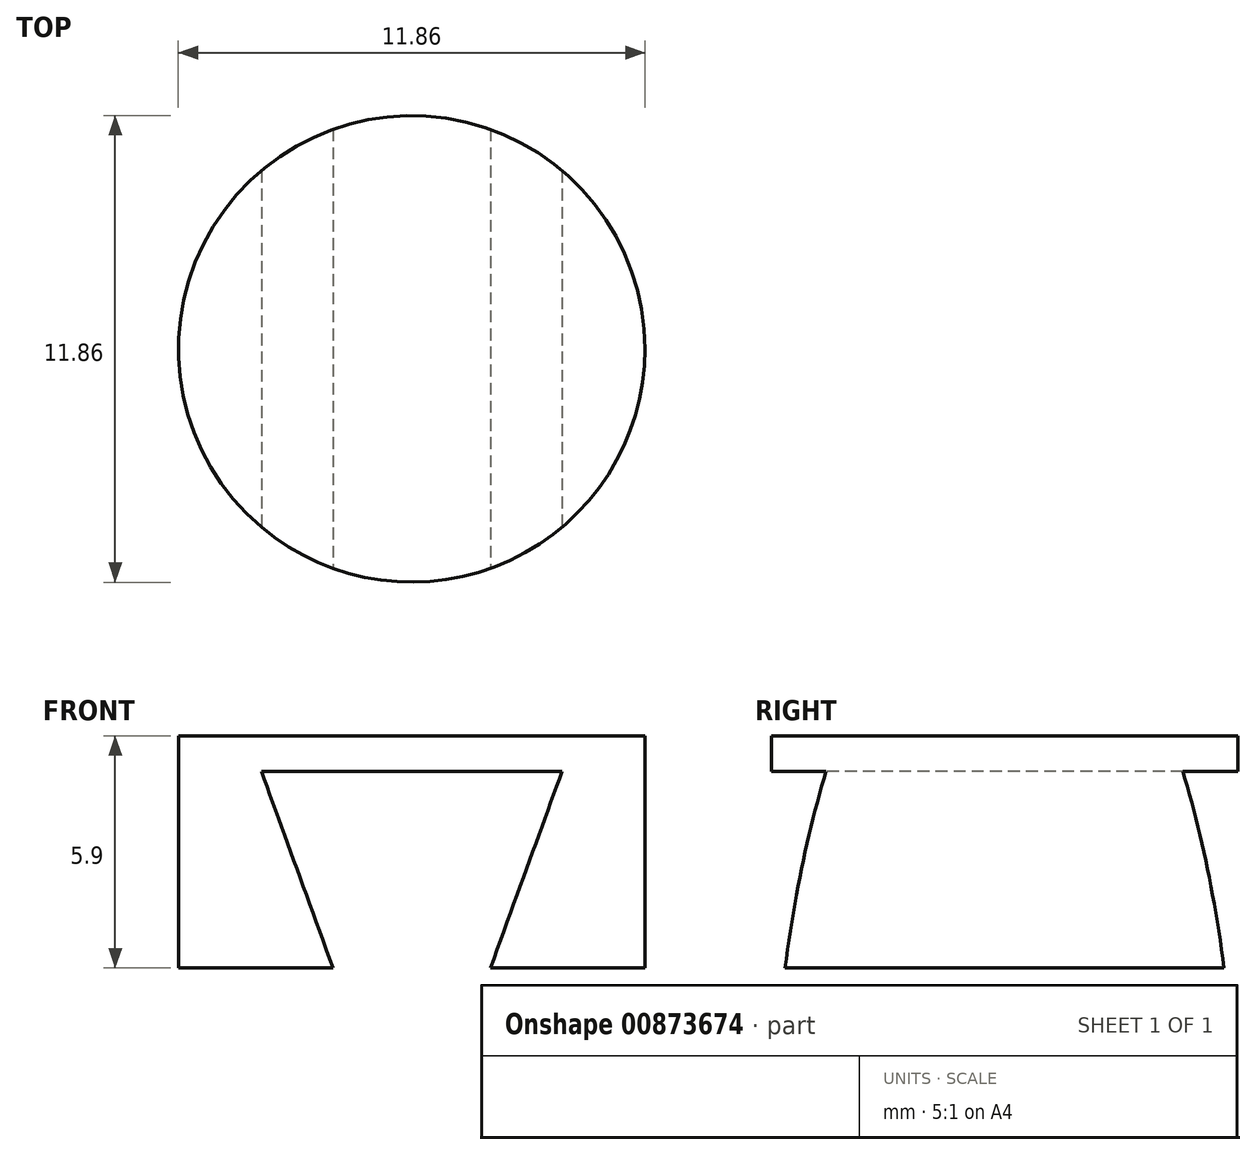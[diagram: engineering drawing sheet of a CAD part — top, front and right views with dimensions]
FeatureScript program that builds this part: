
annotation { "Feature Type Name" : "Feature", "Feature Type Description" : "" }
export const myFeature = defineFeature(function(context is Context, id is Id, definition is map)
    precondition{}
    {
        {
            var Q0;
            Q0=qCreatedBy(makeId("Top.planeOp"),FACE);
            var sketch = newSketch(context, id + "F0", { "sketchPlane" : qUnion([Q0])});
            skCircle(sketch, "E0", {"center": v(0, 0) * mm, "radius": 5.93 * mm});
            skSolve(sketch);
        }
        {
            var Q0;
            Q0=qSketchRegion(id+"F0",true);
            extrude(context, id + "F1", {"entities" : qUnion([Q0]), "depth" : 5.9 * mm, "offsetDistance" : 25 * mm});
        }
        {
            var Q0;
            Q0=qCreatedBy(makeId("Front.planeOp"),FACE);
            var sketch = newSketch(context, id + "F2", { "sketchPlane" : qUnion([Q0])});
            skLineSegment(sketch, "E1", {"start": v(0, 0) * mm, "end": v(2, 0) * mm});
            skLineSegment(sketch, "E2", {"start": v(2, 0) * mm, "end": v(0, 0) * mm});
            skLineSegment(sketch, "E3", {"start": v(0, 0) * mm, "end": v(-2, 0) * mm});
            skLineSegment(sketch, "E4", {"start": v(2, 0) * mm, "end": v(3.82, 5) * mm});
            skLineSegment(sketch, "E5", {"start": v(3.82, 5) * mm, "end": v(-3.82, 5) * mm});
            skLineSegment(sketch, "E6", {"start": v(-3.82, 5) * mm, "end": v(-2, 0) * mm});
            skSolve(sketch);
        }
        {
            var Q0;
            Q0=qSketchRegion(id+"F2",true);
            extrude(context, id + "F3", {"entities" : qUnion([Q0]), "operationType" : NewBodyOperationType.REMOVE, "endBound" : BoundingType.SYMMETRIC, "oppositeDirection" : true, "depth" : 25 * mm, "offsetDistance" : 25 * mm});
        }
    });
